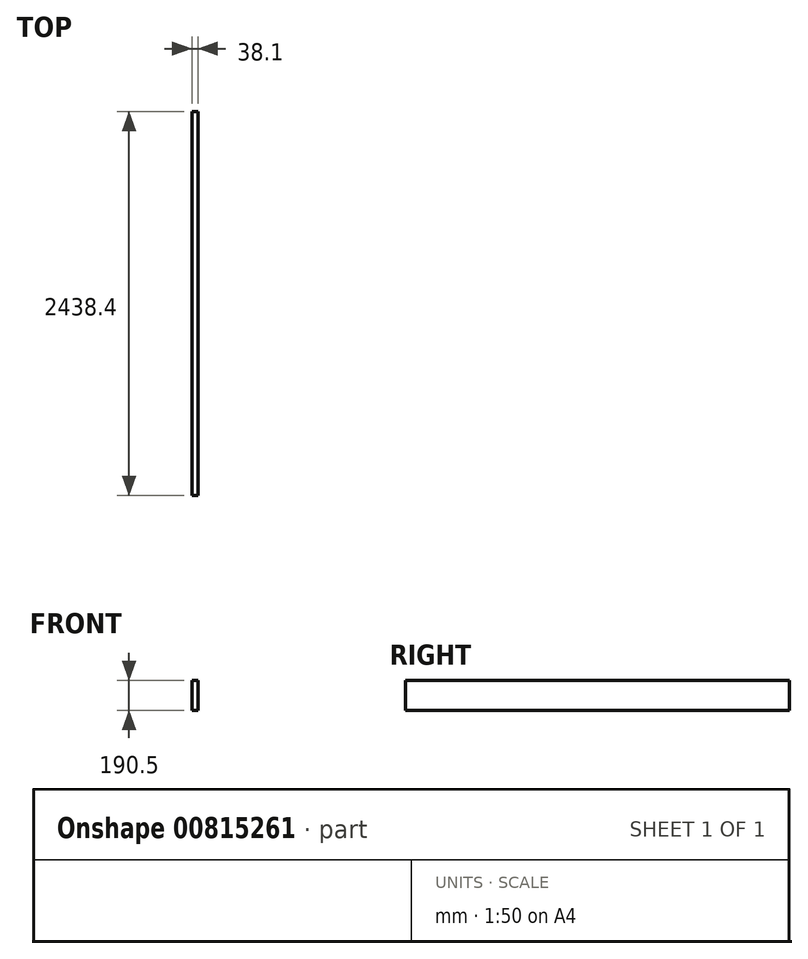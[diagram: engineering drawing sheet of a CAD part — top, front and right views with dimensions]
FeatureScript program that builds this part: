
annotation { "Feature Type Name" : "Feature", "Feature Type Description" : "" }
export const myFeature = defineFeature(function(context is Context, id is Id, definition is map)
    precondition{}
    {
        {
            var Q0;
            Q0=qCreatedBy(makeId("Front.planeOp"),FACE);
            var sketch = newSketch(context, id + "F0", { "sketchPlane" : qUnion([Q0])});
            skLineSegment(sketch, "E0.bottom", {"start": v(-19.05, 95.25) * mm, "end": v(19.05, 95.25) * mm});
            skLineSegment(sketch, "E0.top", {"start": v(-19.05, -95.25) * mm, "end": v(19.05, -95.25) * mm});
            skLineSegment(sketch, "E0.left", {"start": v(-19.05, 95.25) * mm, "end": v(-19.05, -95.25) * mm});
            skLineSegment(sketch, "E0.right", {"start": v(19.05, 95.25) * mm, "end": v(19.05, -95.25) * mm});
            skSolve(sketch);
        }
        {
            var Q0;
            Q0 = qSketchRegion(id + "F0", true);
            extrude(context, id + "F1", {"entities" : qUnion([Q0]), "endBound" : BoundingType.SYMMETRIC, "depth" : 2438.4 * mm, "offsetDistance" : 25.4 * mm});
        }
    });
